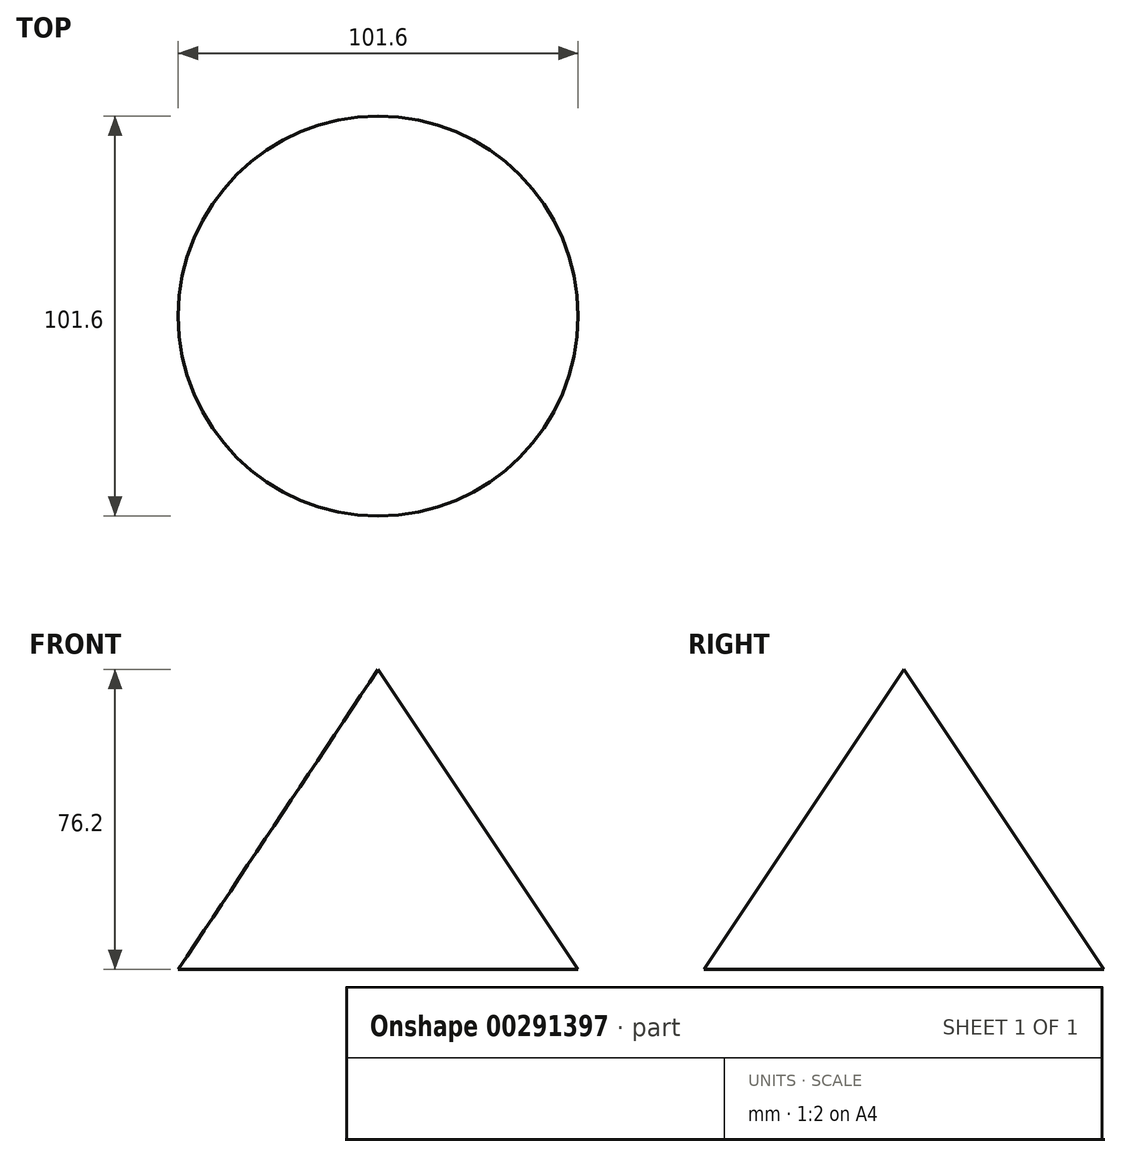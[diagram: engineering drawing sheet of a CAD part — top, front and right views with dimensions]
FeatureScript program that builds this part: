
annotation { "Feature Type Name" : "Feature", "Feature Type Description" : "" }
export const myFeature = defineFeature(function(context is Context, id is Id, definition is map)
    precondition{}
    {
        {
            var Q0;
            Q0=qCreatedBy(makeId("Front.planeOp"),FACE);
            var sketch = newSketch(context, id + "F0", { "sketchPlane" : qUnion([Q0])});
            skLineSegment(sketch, "E0", {"start": v(0, 0) * mm, "end": v(0, 76.2) * mm});
            skLineSegment(sketch, "E1.0", {"start": v(0, 0) * mm, "end": v(50.8, 0) * mm});
            skLineSegment(sketch, "E2", {"start": v(0, 76.2) * mm, "end": v(50.8, 0) * mm});
            skPoint(sketch, "E3.orphan", {"position": v(-51.45, 0) * mm});
            skSolve(sketch);
        }
        {
            var Q0;
            Q0=makeQuery(id+"F0.imprint","IMPRINT",FACE,{"disambiguationData":[TD([[makeQuery(id+"F0.imprint","IMPRINT",EDGE,{"derivedFrom":sQuery(id+"F0.wireOp",EDGE,"E0")}),-1.0]])]});
            var Q1;
            Q1=sQuery(id+"F0.wireOp",EDGE,"E0");
            revolve(context, id + "F1", {"entities" : qUnion([Q0]), "axis" : qUnion([Q1]), "revolveType" : RevolveType.FULL});
        }
    });
